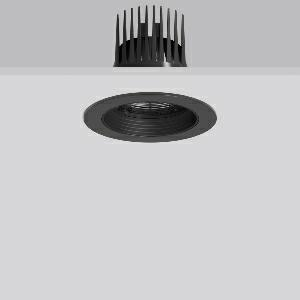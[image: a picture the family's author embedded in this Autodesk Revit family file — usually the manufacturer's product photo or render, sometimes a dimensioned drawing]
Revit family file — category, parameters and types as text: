
# Revit family: heledon_maxi_e_901789_003_2_76_611e
name_source: partatom
category: Lighting Fixtures
units: mm (PartAtom-declared; Revit-internal decimal feet)

## family parameters
Cut with Voids When Loaded = No
Host = Face
Light Source = No
Part Type = Normal
Room Calculation Point = No
Round Connector Dimension = Use Diameter
Shared = No

## types (1)
- HELEDON maxi E (1 x LED Modul 927 bakery, 2850 lm, 2700)
    Apparent Load = 33 VA
    Approval mark = CE
    CIE Flux Codes = 96 99 100 100 100
    Color Rendering = 90
    Color Temperature = 2700
    Default Elevation = 1800 mm
    Description = Series: HELEDON maxi
Round recessed downlight. Housing: die-cast aluminium, powder-coated. Black plastic ring and recessed LED to prevent glare from the side. Optical assembly with lens made of plastic (polycarbonate) for the best homogeneous light distribution - can be changed without tools. Special LED for illumination of pastries included. Suitable for Recessed ceiling mounting. Installation without tools thanks to spring fastening system. Including separate LED converter with connecting cable 600 mm.High quality converter without flickering and stroboscopic effect. Through-wiring box (5 pole) available as accessory. The following accessories can be mounted without use of tools: interchangeable lenses, decorative glasses, honeycomb louvre, clear and frosted diffusers, white interchangeable plastic ring. 
Colour: deep black, matt (RAL 9005)
Diameter: 162 mm
Height: 3 mm
Cut-out diameter: 152 mm
Recess height: 200 mm
Luminaire: recess height: 135 mm
Lamp: LED
Socket: without socket
Colour temperature: bakery
Colour rendering index (CRI): 97
System power: 33 W
Rated luminous flux: 2850 lm
Luminous efficiency: 86 lm/W
Control gear: Converter, dimmable, DALI
Protection class: II
Type of protection: IP 20
    Height = 0 mm  [stored 0 ft]
    Lamp = 1 x LED Modul 927 bakery
    Lamp Light Flux = 2850 lm
    Lamp count = 1
    Length = 162 mm
    Lifetime = 50000 h
    Luminous efficacy = 86 lm/W
    Manufacturer = RZB
    ModVariant = No
    Model = 901789.003.2.76
    Mounting Place = Ceiling
    Mounting Type = Recessed
    Number of Poles = 1
    OnlyDefault = Yes
    Power Factor = 1
    Product Name = HELEDON maxi E
    Product group = Recessed downlights
    ProductGroupID = 402
    Protection Class = Protection class II
    Protection Degree = IP 20
    RLX_Detail_Level = 1
    RLX_Emergency_Light_Flux = 0 lm
    RLX_Emergency_Type = 0
    RLX_Emergency_Type_DB = No
    RlxData = <blob elided: 122593 chars, md5=ae048435>
    Socket = socket
    Standby Power = 0 W
    System Light Flux = 2850 lm
    System Power = 33 W
    Type Comments = Product without accessories
    Type Image = 901663.003.jpg
    URL = http://relux.com
    VarID = ---
    Voltage = 230 V
    Voltage Range = 220-240 V
    Weight = 0.00 kg
    Width = 0 mm  [stored 0 ft]

note: [stored X ft] marks values corroborated as IEEE doubles in the binary element streams (Revit-internal decimal feet)

## geometry (parser evidence)
native form markers: Blend x4, Sweep x10
no freeform markers — native parametric forms only
